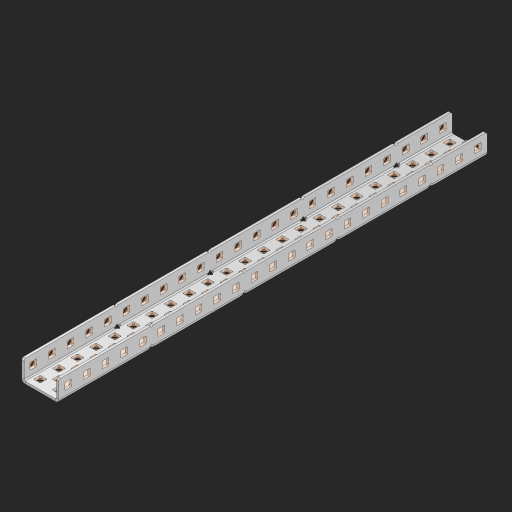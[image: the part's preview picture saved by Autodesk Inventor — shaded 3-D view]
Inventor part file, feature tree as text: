
AUTODESK INVENTOR PART (.ipt)
format: ipt  version: 2023 (Build 270158000, 158)  size: 1,550,848 bytes
history: native  units: in
note: dims shown in document units (in); Inventor stores cm internally (conversion verified against a paired STEP export)
features: other x122, extrude x113, sheet_metal_op x11, sketch x10, pattern_linear x2, mirror x1, chamfer x1
ambient origin geometry x8: Origin, YZ Plane, XZ Plane, XY Plane, X Axis, Y Axis, Z Axis, Center Point
bodies: Solid1 (feature_tree), Body (feature_tree)
feature tree (260):
  sheet_metal_op  "Flanges"
  other  "Flange Pattern Plane"
  other  "Flange Pattern Sketch"
  sheet_metal_op  "Flange Pattern"
  sheet_metal_op  "Body Pattern"
  pattern_linear  "Center Pattern"  Spacing1=0.0625in  [1 undecoded]
  other  "Arc Length"
  mirror  "Notch Mirror"
  pattern_linear  "Notch Pattern"  Spacing1=0.182in  [1 undecoded]
  chamfer  "End Chamfer"
  extrude  "Half Cut"  Depth=0.02in
  sketch  "Sketch1"  dims[d0=1.0in]
  other  "Plate1"
  sketch  "Sketch2"  dims[d1=11.5in]
  other  "Plate2"
  sheet_metal_op  "Bend1"
  sheet_metal_op  "Corner1"
  sketch  "Sketch3"  dims[d2=0.0625in]
  sketch  "Sketch7"  dims[d3=0.0625in]
  other  "Srf1"
  other  "Srf2"
  sketch  "Sketch8"  dims[d4=0.0312in]
  sketch  "Sketch9"  dims[d5=0.125in]
  other  "Srf91"
  sheet_metal_op  "Body Pattern Sketch"
  other  "Srf92"
  sketch  "Sketch13"  dims[d6=0.0625in]
  sketch  "Sketch14"  dims[d7=0.5in d8=90.0deg d9=0.0312in]
  sketch  "Sketch15"  dims[d10=0.25in]
  sketch  "Sketch16"  dims[d11=0.0625in d12=0.0625in d16=0.182in d17=0.02in d18=0.0625in d19=0.0in d20=0.25in d21=0.25in d38=9.0551in d40=0.5in d41=0.7874in d43=1.0in d46=0.172in d47=1.0in d48=0.0in d49=0.182in d50=0.02in d51=0.25in d52=0.25in d53=0.0625in d54=0.0in d55=0.172in d56=1.0in d57=0.0in d58=0.25in d60=9.0551in d62=0.5in d63=0.7874in d65=0.5in d85=0.1473in d86=0.1782in d88=0.04in d89=0.0625in d90=0.0in d91=0.04in d92=0.0491in d95=2.5in d96=0.04in d97=0.25in d98=45.0deg d99=0.25in d100=0.5in d101=0.0in d102=2.497in d106=0.182in d107=0.02in d108=0.5in d109=0.5in d110=0.0625in d111=0.0in d112=0.172in d113=0.5in d114=0.0in d117=0.5in d118=0.5in d119=0.5in]
  other  "Srf786"
  other  "Srf823"
  other  "Srf824"
  other  "Srf825"
  other  "Srf826"
  other  "Srf827"
  other  "Srf828"
  other  "Srf829"
  other  "Srf856"
  other  "Srf857"
  other  "Srf858"
  other  "Srf859"
  other  "Srf860"
  other  "Srf861"
  other  "Srf862"
  other  "Srf889"
  other  "Srf890"
  other  "Srf891"
  other  "Srf892"
  other  "Srf893"
  other  "Srf894"
  other  "Srf895"
  other  "Srf896"
  other  "Srf922"
  other  "Srf923"
  other  "Srf924"
  other  "Srf925"
  other  "Srf926"
  other  "Srf959"
  other  "Srf960"
  other  "Srf961"
  other  "Srf962"
  other  "Srf963"
  other  "Srf996"
  other  "Srf997"
  other  "Srf998"
  other  "Srf999"
  other  "Srf1000"
  other  "Srf1143"
  other  "Srf1144"
  other  "Srf1145"
  other  "Srf1146"
  other  "Srf1147"
  other  "Srf1148"
  other  "Srf1149"
  other  "Srf1150"
  other  "Srf1151"
  other  "Srf1152"
  other  "Srf1153"
  other  "Srf1154"
  other  "Srf1155"
  other  "Srf1156"
  other  "Srf1157"
  other  "Srf1158"
  other  "Srf1159"
  other  "Srf1160"
  other  "Srf1161"
  other  "Srf1162"
  other  "Srf1163"
  other  "Srf1164"
  other  "Srf1165"
  other  "Srf1166"
  other  "Srf1167"
  other  "Srf1168"
  other  "Srf1169"
  other  "Srf1170"
  other  "Srf1171"
  other  "Srf1172"
  other  "Srf1173"
  other  "Srf1174"
  other  "Srf1199"
  other  "Srf1200"
  other  "Srf1201"
  other  "Srf1202"
  other  "Srf1203"
  other  "Srf1204"
  other  "Srf1205"
  other  "Srf1206"
  other  "Srf1207"
  other  "Srf1208"
  other  "Srf1209"
  other  "Srf1210"
  other  "Srf1211"
  other  "Srf1212"
  other  "Srf1213"
  other  "Srf1214"
  other  "Srf1215"
  other  "Srf1216"
  other  "Srf1217"
  other  "Srf1218"
  other  "Srf1219"
  other  "Srf1220"
  other  "Srf1221"
  other  "Srf1222"
  other  "Srf1223"
  other  "Srf1224"
  other  "Srf1225"
  other  "Srf1226"
  other  "Srf1227"
  other  "Srf1228"
  other  "Srf1229"
  other  "Srf1230"
  other  "Srf1255"
  other  "Srf1256"
  other  "Srf1257"
  other  "Srf1258"
  other  "Srf1259"
  other  "Srf1260"
  other  "Srf1261"
  other  "Srf1262"
  other  "Srf1263"
  sheet_metal_op  "Flange Stamp"
  sheet_metal_op  "Flange Circle"
  sheet_metal_op  "Body Stamp"
  sheet_metal_op  "Body Circle"
  other  "Center Stamp"
  other  "Center Circle"
  sheet_metal_op  "Notch"
  extrude  "ExtrusionSrf2"  Depth=0.0625in
  extrude  "ExtrusionSrf92"  TaperAngle=0.0deg  [1 undecoded]
  extrude  "ExtrusionSrf823"  Depth=0.5in
  extrude  "ExtrusionSrf824"  Depth=0.5in
  extrude  "ExtrusionSrf825"  Depth=0.5in
  extrude  "ExtrusionSrf826"  Depth=0.5in
  extrude  "ExtrusionSrf827"  Depth=1.0in TaperAngle=0.0deg
  extrude  "ExtrusionSrf828"  Depth=0.5in
  extrude  "ExtrusionSrf829"  Depth=0.02in
  extrude  "ExtrusionSrf856"  Depth=0.5in
  extrude  "ExtrusionSrf857"  Depth=0.5in
  extrude  "ExtrusionSrf858"  Depth=0.0625in
  extrude  "ExtrusionSrf859"  TaperAngle=0.0deg  [1 undecoded]
  extrude  "ExtrusionSrf860"  Depth=0.5in
  extrude  "ExtrusionSrf861"  Depth=1.0in TaperAngle=0.0deg
  extrude  "ExtrusionSrf862"  Depth=0.5in
  extrude  "ExtrusionSrf889"  Depth=0.5in
  extrude  "ExtrusionSrf890"  Depth=0.5in
  extrude  "ExtrusionSrf891"  Depth=0.5in
  extrude  "ExtrusionSrf892"  Depth=0.5in
  extrude  "ExtrusionSrf893"  Depth=0.5in
  extrude  "ExtrusionSrf894"  Depth=0.0625in
  extrude  "ExtrusionSrf895"  TaperAngle=0.0deg  [1 undecoded]
  extrude  "ExtrusionSrf896"  Depth=0.5in
  extrude  "ExtrusionSrf922"  Depth=0.5in
  extrude  "ExtrusionSrf923"  Depth=2.5in
  extrude  "ExtrusionSrf924"  Depth=0.5in TaperAngle=45.0deg
  extrude  "ExtrusionSrf925"  Depth=0.5in
  extrude  "ExtrusionSrf926"  Depth=0.5in TaperAngle=0.0deg
  extrude  "ExtrusionSrf959"  Depth=0.5in
  extrude  "ExtrusionSrf960"  Depth=0.5in
  extrude  "ExtrusionSrf961"  Depth=0.02in
  extrude  "ExtrusionSrf962"  Depth=0.5in
  extrude  "ExtrusionSrf963"  Depth=0.5in
  extrude  "ExtrusionSrf996"  Depth=0.0625in
  extrude  "ExtrusionSrf997"  TaperAngle=0.0deg  [1 undecoded]
  extrude  "ExtrusionSrf998"  Depth=0.5in
  extrude  "ExtrusionSrf999"  Depth=0.5in TaperAngle=0.0deg
  extrude  "ExtrusionSrf1000"  Depth=0.5in
  extrude  "ExtrusionSrf1143"  Depth=0.5in
  extrude  "ExtrusionSrf1144"  Depth=0.5in
  extrude  "ExtrusionSrf1145"  [1 undecoded]
  extrude  "ExtrusionSrf1146"  [1 undecoded]
  extrude  "ExtrusionSrf1147"  [1 undecoded]
  extrude  "ExtrusionSrf1148"  [1 undecoded]
  extrude  "ExtrusionSrf1149"  [1 undecoded]
  extrude  "ExtrusionSrf1150"  [1 undecoded]
  extrude  "ExtrusionSrf1151"  [1 undecoded]
  extrude  "ExtrusionSrf1152"  [1 undecoded]
  extrude  "ExtrusionSrf1153"  [1 undecoded]
  extrude  "ExtrusionSrf1154"  [1 undecoded]
  extrude  "ExtrusionSrf1155"  [1 undecoded]
  extrude  "ExtrusionSrf1156"  [1 undecoded]
  extrude  "ExtrusionSrf1157"  [1 undecoded]
  extrude  "ExtrusionSrf1158"  [1 undecoded]
  extrude  "ExtrusionSrf1159"  [1 undecoded]
  extrude  "ExtrusionSrf1160"  [1 undecoded]
  extrude  "ExtrusionSrf1161"  [1 undecoded]
  extrude  "ExtrusionSrf1162"  [1 undecoded]
  extrude  "ExtrusionSrf1163"  [1 undecoded]
  extrude  "ExtrusionSrf1164"  [1 undecoded]
  extrude  "ExtrusionSrf1165"  [1 undecoded]
  extrude  "ExtrusionSrf1166"  [1 undecoded]
  extrude  "ExtrusionSrf1167"  [1 undecoded]
  extrude  "ExtrusionSrf1168"  [1 undecoded]
  extrude  "ExtrusionSrf1169"  [1 undecoded]
  extrude  "ExtrusionSrf1170"  [1 undecoded]
  extrude  "ExtrusionSrf1171"  [1 undecoded]
  extrude  "ExtrusionSrf1172"  [1 undecoded]
  extrude  "ExtrusionSrf1173"  [1 undecoded]
  extrude  "ExtrusionSrf1174"  [1 undecoded]
  extrude  "ExtrusionSrf1199"  [1 undecoded]
  extrude  "ExtrusionSrf1200"  [1 undecoded]
  extrude  "ExtrusionSrf1201"  [1 undecoded]
  extrude  "ExtrusionSrf1202"  [1 undecoded]
  extrude  "ExtrusionSrf1203"  [1 undecoded]
  extrude  "ExtrusionSrf1204"  [1 undecoded]
  extrude  "ExtrusionSrf1205"  [1 undecoded]
  extrude  "ExtrusionSrf1206"  [1 undecoded]
  extrude  "ExtrusionSrf1207"  [1 undecoded]
  extrude  "ExtrusionSrf1208"  [1 undecoded]
  extrude  "ExtrusionSrf1209"  [1 undecoded]
  extrude  "ExtrusionSrf1210"  [1 undecoded]
  extrude  "ExtrusionSrf1211"  [1 undecoded]
  extrude  "ExtrusionSrf1212"  [1 undecoded]
  extrude  "ExtrusionSrf1213"  [1 undecoded]
  extrude  "ExtrusionSrf1214"  [1 undecoded]
  extrude  "ExtrusionSrf1215"  [1 undecoded]
  extrude  "ExtrusionSrf1216"  [1 undecoded]
  extrude  "ExtrusionSrf1217"  [1 undecoded]
  extrude  "ExtrusionSrf1218"  [1 undecoded]
  extrude  "ExtrusionSrf1219"  [1 undecoded]
  extrude  "ExtrusionSrf1220"  [1 undecoded]
  extrude  "ExtrusionSrf1221"  [1 undecoded]
  extrude  "ExtrusionSrf1222"  [1 undecoded]
  extrude  "ExtrusionSrf1223"  [1 undecoded]
  extrude  "ExtrusionSrf1224"  [1 undecoded]
  extrude  "ExtrusionSrf1225"  [1 undecoded]
  extrude  "ExtrusionSrf1226"  [1 undecoded]
  extrude  "ExtrusionSrf1227"  [1 undecoded]
  extrude  "ExtrusionSrf1228"  [1 undecoded]
  extrude  "ExtrusionSrf1229"  [1 undecoded]
  extrude  "ExtrusionSrf1230"  [1 undecoded]
  extrude  "ExtrusionSrf1255"  [1 undecoded]
  extrude  "ExtrusionSrf1256"  [1 undecoded]
  extrude  "ExtrusionSrf1257"  [1 undecoded]
  extrude  "ExtrusionSrf1258"  [1 undecoded]
  extrude  "ExtrusionSrf1259"  [1 undecoded]
  extrude  "ExtrusionSrf1260"  [1 undecoded]
  extrude  "ExtrusionSrf1261"  [1 undecoded]
  extrude  "ExtrusionSrf1262"  [1 undecoded]
  extrude  "ExtrusionSrf1263"  [1 undecoded]
note: 77 required parameter values undecoded (feature->parameter linkage not recoverable at this tier; creation-order binding heuristic only, values carry confidence <= 0.55)
